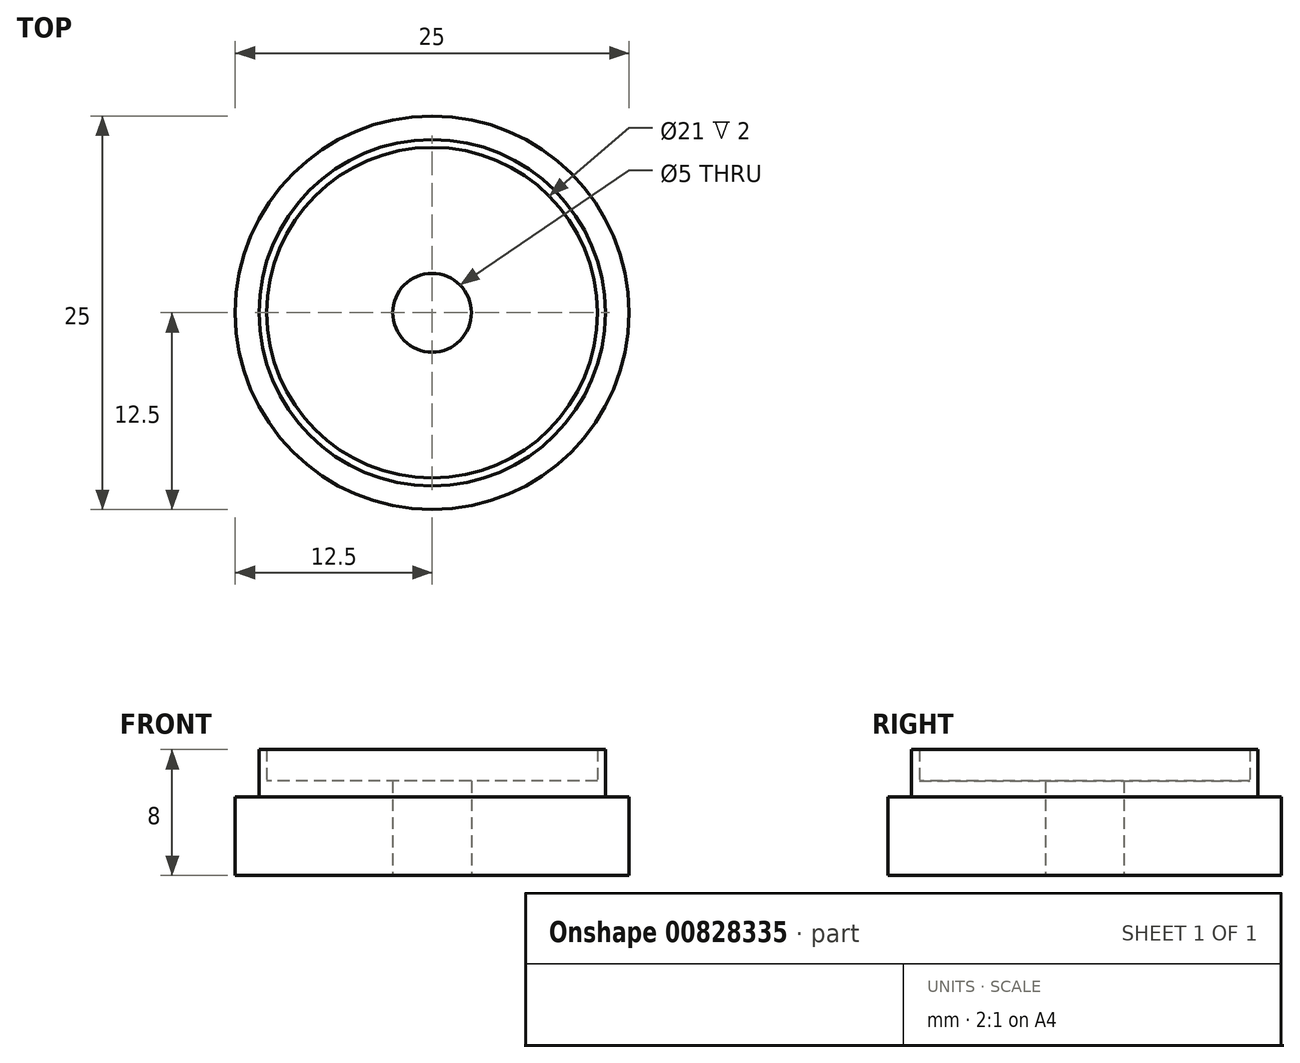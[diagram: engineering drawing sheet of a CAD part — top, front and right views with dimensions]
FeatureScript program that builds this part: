
annotation { "Feature Type Name" : "Feature", "Feature Type Description" : "" }
export const myFeature = defineFeature(function(context is Context, id is Id, definition is map)
    precondition{}
    {
        {
            var Q0;
            Q0=qCreatedBy(makeId("Top.planeOp"),FACE);
            var sketch = newSketch(context, id + "F0", { "sketchPlane" : qUnion([Q0])});
            skCircle(sketch, "E0", {"center": v(0, 0) * mm, "radius": 12.5 * mm});
            skCircle(sketch, "E1", {"center": v(0, 0) * mm, "radius": 11 * mm});
            skCircle(sketch, "E2", {"center": v(0, 0) * mm, "radius": 10.5 * mm});
            skSolve(sketch);
        }
        {
            var Q0;
            Q0 = qSketchRegion(id + "F0", true);
            extrude(context, id + "F1", {"entities" : qUnion([Q0]), "depth" : 5 * mm, "offsetDistance" : 25 * mm});
        }
        {
            var Q0;
            Q0=makeQuery(id+"F0.imprint","IMPRINT",FACE,{"disambiguationData":[TD([[makeQuery(id+"F0.imprint","IMPRINT",EDGE,{"derivedFrom":sQuery(id+"F0.wireOp",EDGE,"E1")}),1.0]])]});
            extrude(context, id + "F2", {"entities" : qUnion([Q0]), "operationType" : NewBodyOperationType.ADD, "depth" : 8 * mm, "offsetDistance" : 25 * mm});
        }
        {
            var Q0;
            Q0=makeQuery(id+"F0.imprint","IMPRINT",FACE,{"disambiguationData":[TD([[makeQuery(id+"F0.imprint","IMPRINT",EDGE,{"derivedFrom":sQuery(id+"F0.wireOp",EDGE,"E2")}),1.0]])]});
            extrude(context, id + "F3", {"entities" : qUnion([Q0]), "operationType" : NewBodyOperationType.ADD, "depth" : 6 * mm, "offsetDistance" : 25 * mm});
        }
        {
            var Q0;
            Q0=sQuery(id+"F0.wireOp",VERTEX,"E1.center");
            var Q1;
            Q1=makeQuery(id+"F1.opExtrude","SWEPT_BODY",BODY,{"disambiguationData":[OSD([sQuery(id+"F0.wireOp",EDGE,"E0"),sQuery(id+"F0.wireOp",EDGE,"E1")])]});
            hole(context, id + "F4", {"style" : HoleStyle.SIMPLE, "endStyle" : HoleEndStyle.THROUGH, "oppositeDirection" : true, "holeDiameter" : 5 * mm, "majorDiameter" : 5 * mm, "isTappedThrough" : true, "tappedDepth" : 12 * mm, "tapClearance" : 3, "locations" : qUnion([Q0]), "scope" : qUnion([Q1])});
        }
    });
